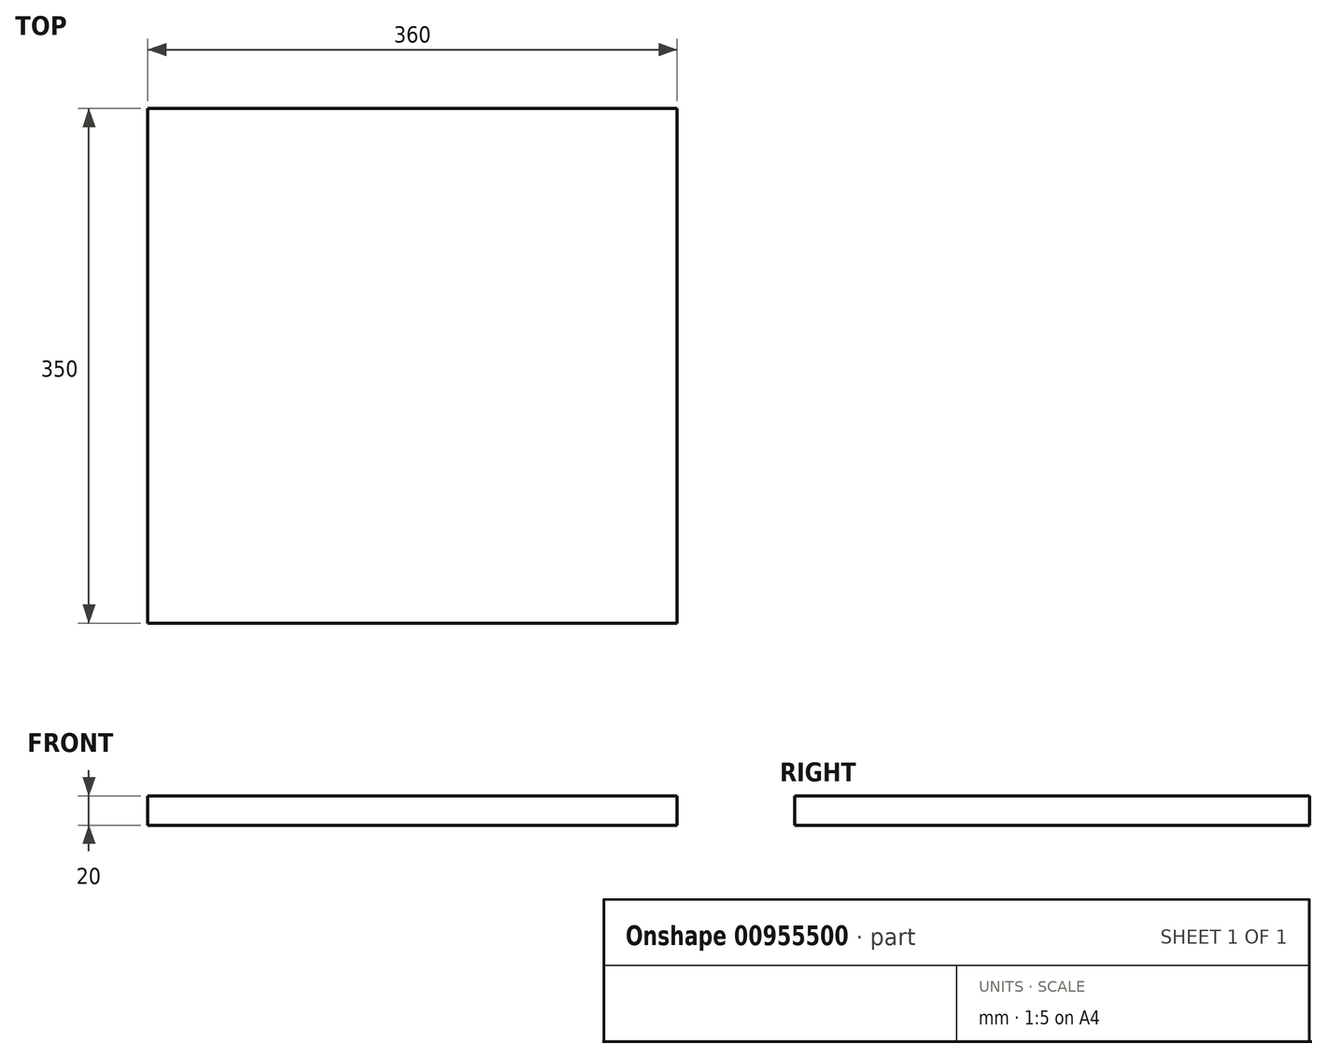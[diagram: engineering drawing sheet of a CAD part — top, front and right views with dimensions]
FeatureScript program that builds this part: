
annotation { "Feature Type Name" : "Feature", "Feature Type Description" : "" }
export const myFeature = defineFeature(function(context is Context, id is Id, definition is map)
    precondition{}
    {
        {
            var Q0;
            Q0=qCreatedBy(makeId("Top.planeOp"),FACE);
            var sketch = newSketch(context, id + "F0", { "sketchPlane" : qUnion([Q0])});
            skLineSegment(sketch, "E0", {"start": v(0, 0) * mm, "end": v(360, 0) * mm});
            skLineSegment(sketch, "E1", {"start": v(360, 0) * mm, "end": v(360, 350) * mm});
            skLineSegment(sketch, "E2", {"start": v(360, 350) * mm, "end": v(0, 350) * mm});
            skLineSegment(sketch, "E3", {"start": v(0, 350) * mm, "end": v(0, 0) * mm});
            skSolve(sketch);
        }
        {
            var Q0;
            Q0=makeQuery(id+"F0.imprint","IMPRINT",FACE,{"disambiguationData":[TD([[makeQuery(id+"F0.imprint","IMPRINT",EDGE,{"derivedFrom":sQuery(id+"F0.wireOp",EDGE,"E0")}),1.0]])]});
            extrude(context, id + "F1", {"entities" : qUnion([Q0]), "depth" : 20 * mm, "offsetDistance" : 25 * mm});
        }
    });
